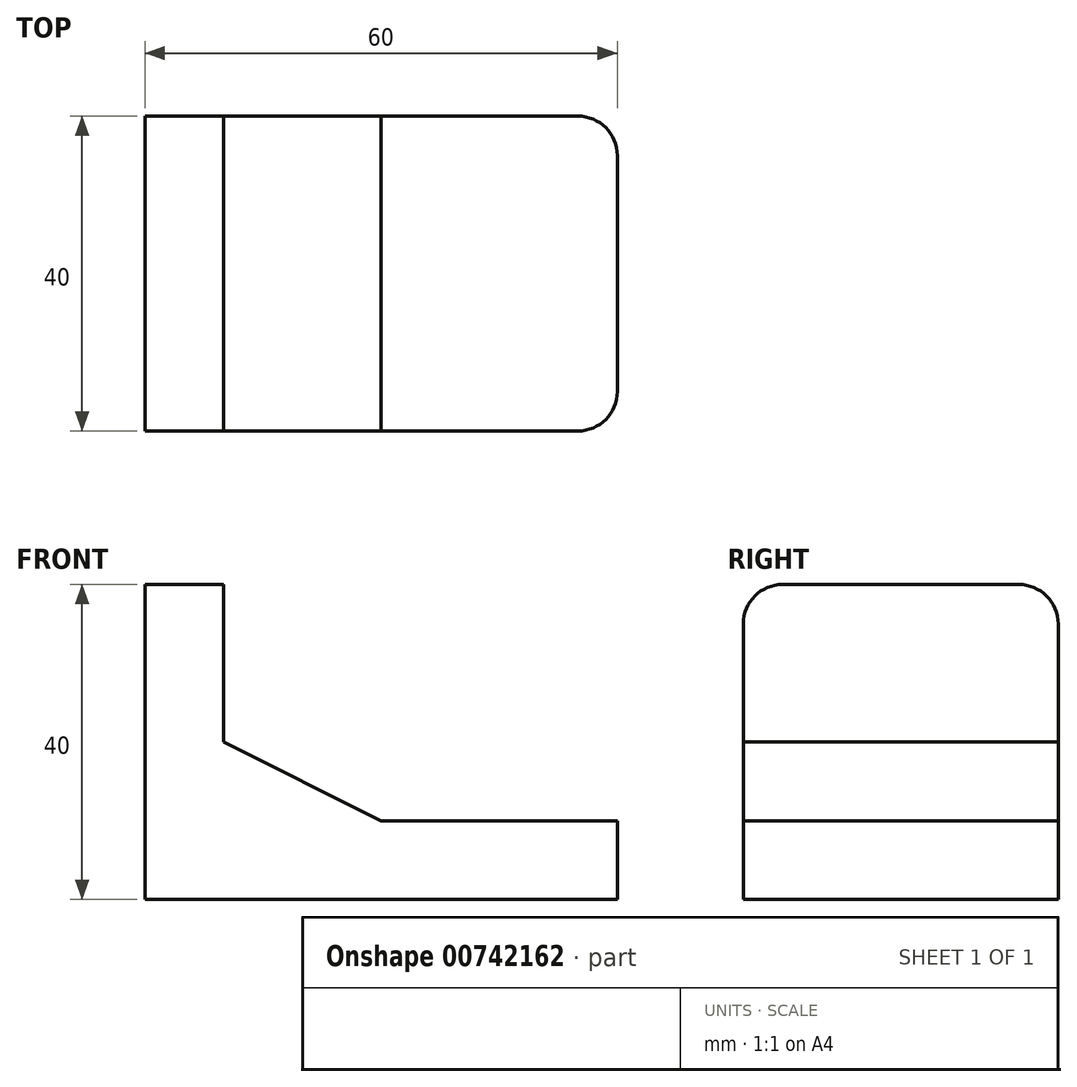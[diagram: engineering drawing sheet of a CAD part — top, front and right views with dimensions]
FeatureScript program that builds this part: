
annotation { "Feature Type Name" : "Feature", "Feature Type Description" : "" }
export const myFeature = defineFeature(function(context is Context, id is Id, definition is map)
    precondition{}
    {
        {
            var Q0;
            Q0=qCreatedBy(makeId("Front.planeOp"),FACE);
            var sketch = newSketch(context, id + "F0", { "sketchPlane" : qUnion([Q0])});
            skLineSegment(sketch, "E0", {"start": v(0, 0) * mm, "end": v(-20, 10) * mm});
            skLineSegment(sketch, "E1", {"start": v(-20, 10) * mm, "end": v(-20, 30) * mm});
            skLineSegment(sketch, "E2", {"start": v(-20, 30) * mm, "end": v(-30, 30) * mm});
            skLineSegment(sketch, "E3", {"start": v(-30, 30) * mm, "end": v(-30, -10) * mm});
            skLineSegment(sketch, "E4", {"start": v(-30, -10) * mm, "end": v(30, -10) * mm});
            skLineSegment(sketch, "E5", {"start": v(30, -10) * mm, "end": v(30, 0) * mm});
            skLineSegment(sketch, "E6", {"start": v(30, 0) * mm, "end": v(0, 0) * mm});
            skSolve(sketch);
        }
        {
            var Q0;
            Q0 = qSketchRegion(id + "F0", true);
            extrude(context, id + "F1", {"entities" : qUnion([Q0]), "depth" : 40 * mm, "offsetDistance" : 25 * mm});
        }
        {
            var Q0;
            Q0=makeQuery(id+"F1.opExtrude","CAP_EDGE",EDGE,{"disambiguationData":[OSD([sQuery(id+"F0.wireOp",EDGE,"E5")])],"isStart":false});
            var Q1;
            Q1=makeQuery(id+"F1.opExtrude","CAP_EDGE",EDGE,{"disambiguationData":[OSD([sQuery(id+"F0.wireOp",EDGE,"E5")])],"isStart":true});
            var Q2;
            Q2=makeQuery(id+"F1.opExtrude","CAP_EDGE",EDGE,{"disambiguationData":[OSD([sQuery(id+"F0.wireOp",EDGE,"E2")])],"isStart":false});
            var Q3;
            Q3=makeQuery(id+"F1.opExtrude","CAP_EDGE",EDGE,{"disambiguationData":[OSD([sQuery(id+"F0.wireOp",EDGE,"E2")])],"isStart":true});
            fillet(context, id + "F2", {"entities" : qUnion([Q0, Q1, Q2, Q3]), "radius" : 5 * mm, "tangentPropagation" : true, "allowEdgeOverflow" : false});
        }
    });
